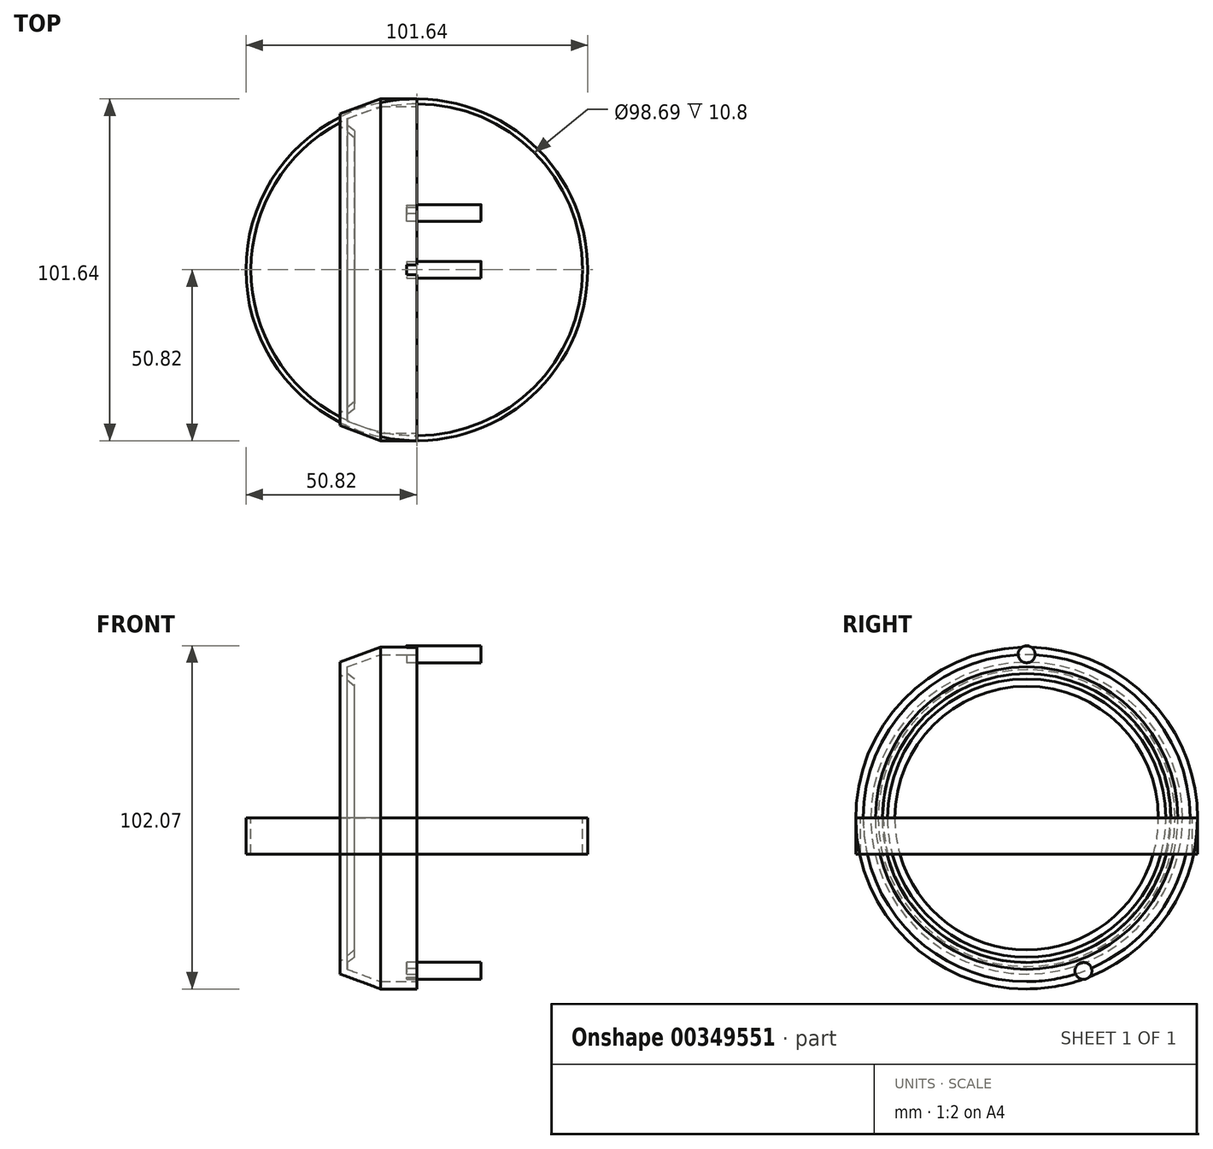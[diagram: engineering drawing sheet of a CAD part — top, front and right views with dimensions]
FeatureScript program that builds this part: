
annotation { "Feature Type Name" : "Feature", "Feature Type Description" : "" }
export const myFeature = defineFeature(function(context is Context, id is Id, definition is map)
    precondition{}
    {
        {
            var Q0;
            Q0=qCreatedBy(makeId("Top.planeOp"),FACE);
            var sketch = newSketch(context, id + "F0", { "sketchPlane" : qUnion([Q0])});
            skCircle(sketch, "E0", {"center": v(0, 0) * mm, "radius": 50.81 * mm});
            skCircle(sketch, "E1", {"center": v(0, 0) * mm, "radius": 49.34 * mm});
            skSolve(sketch);
        }
        {
            var Q0;
            Q0=makeQuery(id+"F0.imprint","IMPRINT",FACE,{"disambiguationData":[TD([[makeQuery(id+"F0.imprint","IMPRINT",EDGE,{"derivedFrom":sQuery(id+"F0.wireOp",EDGE,"E0")}),1.0]])]});
            extrude(context, id + "F1", {"entities" : qUnion([Q0]), "oppositeDirection" : true, "depth" : 10.8 * mm});
        }
        {
            var Q0;
            Q0=qCreatedBy(makeId("Front.planeOp"),FACE);
            var sketch = newSketch(context, id + "F2", { "sketchPlane" : qUnion([Q0])});
            skLineSegment(sketch, "E2", {"start": v(0, 50.81) * mm, "end": v(-10.8, 50.81) * mm});
            skLineSegment(sketch, "E3", {"start": v(-10.8, 48.62) * mm, "end": v(0, 48.62) * mm});
            skLineSegment(sketch, "E4", {"start": v(0, 48.62) * mm, "end": v(0, 50.81) * mm});
            skLineSegment(sketch, "E5", {"start": v(-10.8, 50.81) * mm, "end": v(-22.8, 46.36) * mm});
            skLineSegment(sketch, "E6", {"start": v(-10.8, 48.62) * mm, "end": v(-22.8, 44.16) * mm});
            skLineSegment(sketch, "E7", {"start": v(-22.8, 44.16) * mm, "end": v(-22.8, 46.36) * mm});
            skLineSegment(sketch, "E8", {"start": v(-22.8, 46.36) * mm, "end": v(-22.8, 42.68) * mm});
            skLineSegment(sketch, "E9", {"start": v(-22.8, 42.68) * mm, "end": v(-18.54, 39.19) * mm});
            skLineSegment(sketch, "E10", {"start": v(-18.54, 39.19) * mm, "end": v(-18.54, 41.39) * mm});
            skLineSegment(sketch, "E11", {"start": v(-20.6, 44.16) * mm, "end": v(-20.6, 47.18) * mm});
            skLineSegment(sketch, "E12", {"start": v(-20.6, 47.18) * mm, "end": v(-20.6, 44.16) * mm});
            skLineSegment(sketch, "E13", {"start": v(-20.6, 47.18) * mm, "end": v(-20.67, 40.93) * mm});
            skLineSegment(sketch, "E14", {"start": v(-18.54, 41.39) * mm, "end": v(-22.8, 44.52) * mm});
            skLineSegment(sketch, "E15", {"start": v(0, 0) * mm, "end": v(-21.95, 0) * mm});
            skSolve(sketch);
        }
        {
            var Q0;
            {var subQ1=sQuery(id+"F2.wireOp",EDGE,"E2");Q0=makeQuery(id+"F2.imprint","IMPRINT",FACE,{"disambiguationData":[TD([[makeQuery(id+"F2.imprint","IMPRINT",EDGE,{"derivedFrom":subQ1}),1.0]])]});}
            var Q1;
            {var subQ5=sQuery(id+"F2.wireOp",EDGE,"E8");var subQ7=sQuery(id+"F2.wireOp",EDGE,"E6");var subQ8=makeQuery(id+"F2.imprint","INTERSECT",VERTEX,{"derivedFrom":[subQ7,subQ5]});Q1=makeQuery(id+"F2.imprint","IMPRINT",FACE,{"disambiguationData":[TD([[makeQuery(id+"F2.imprint","IMPRINT",EDGE,{"disambiguationData":[TD([[subQ8,1.0]])],"derivedFrom":subQ7}),1.0]])]});}
            var Q2;
            {var subQ0=sQuery(id+"F2.wireOp",EDGE,"E10");Q2=makeQuery(id+"F2.imprint","IMPRINT",FACE,{"disambiguationData":[TD([[makeQuery(id+"F2.imprint","IMPRINT",EDGE,{"derivedFrom":subQ0}),1.0]])]});}
            var Q3;
            {var subQ0=sQuery(id+"F2.wireOp",EDGE,"E13");var subQ1=sQuery(id+"F2.wireOp",EDGE,"E6");var subQ2=makeQuery(id+"F2.imprint","INTERSECT",VERTEX,{"derivedFrom":[subQ1,subQ0]});Q3=makeQuery(id+"F2.imprint","IMPRINT",FACE,{"disambiguationData":[TD([[makeQuery(id+"F2.imprint","IMPRINT",EDGE,{"disambiguationData":[TD([[subQ2,-1.0]])],"derivedFrom":subQ1}),1.0]])]});}
            var Q4;
            {var subQ0=sQuery(id+"F2.wireOp",EDGE,"E13");var subQ3=sQuery(id+"F2.wireOp",EDGE,"E6");var subQ4=makeQuery(id+"F2.imprint","INTERSECT",VERTEX,{"derivedFrom":[subQ3,subQ0]});Q4=makeQuery(id+"F2.imprint","IMPRINT",FACE,{"disambiguationData":[TD([[makeQuery(id+"F2.imprint","IMPRINT",EDGE,{"disambiguationData":[TD([[subQ4,-1.0]])],"derivedFrom":subQ3}),-1.0]])]});}
            var Q5;
            {var subQ0=sQuery(id+"F2.wireOp",EDGE,"E8");var subQ1=sQuery(id+"F2.wireOp",EDGE,"E6");var subQ2=makeQuery(id+"F2.imprint","INTERSECT",VERTEX,{"derivedFrom":[subQ1,subQ0]});Q5=makeQuery(id+"F2.imprint","IMPRINT",FACE,{"disambiguationData":[TD([[makeQuery(id+"F2.imprint","IMPRINT",EDGE,{"disambiguationData":[TD([[subQ2,1.0]])],"derivedFrom":subQ1}),-1.0]])]});}
            var Q6;
            {var subQ0=sQuery(id+"F2.wireOp",EDGE,"E7");Q6=makeQuery(id+"F2.imprint","IMPRINT",FACE,{"disambiguationData":[TD([[makeQuery(id+"F2.imprint","IMPRINT",EDGE,{"derivedFrom":subQ0}),-1.0]])]});}
            var Q7;
            {var subQ0=sQuery(id+"F2.wireOp",EDGE,"E12");var subQ1=sQuery(id+"F2.wireOp",EDGE,"E6");var subQ2=makeQuery(id+"F2.imprint","INTERSECT",VERTEX,{"derivedFrom":[subQ1,subQ0]});Q7=makeQuery(id+"F2.imprint","IMPRINT",FACE,{"disambiguationData":[TD([[makeQuery(id+"F2.imprint","IMPRINT",EDGE,{"disambiguationData":[TD([[subQ2,-1.0]])],"derivedFrom":subQ1}),-1.0]])]});}
            var Q8;
            Q8=sQuery(id+"F2.wireOp",EDGE,"E15");
            revolve(context, id + "F3", {"entities" : qUnion([Q0, Q1, Q2, Q3, Q4, Q5, Q6, Q7]), "axis" : qUnion([Q8]), "revolveType" : RevolveType.FULL});
        }
        {
            var Q0;
            Q0=qCreatedBy(makeId("Right.planeOp"),FACE);
            var sketch = newSketch(context, id + "F4", { "sketchPlane" : qUnion([Q0])});
            skCircle(sketch, "E16", {"center": v(0, 48.72) * mm, "radius": 2.52 * mm});
            skSolve(sketch);
        }
        {
            var Q0;
            Q0=makeQuery(id+"F4.imprint","IMPRINT",FACE,{"disambiguationData":[TD([[makeQuery(id+"F4.imprint","IMPRINT",EDGE,{"derivedFrom":sQuery(id+"F4.wireOp",EDGE,"E16")}),1.0]])]});
            extrude(context, id + "F5", {"entities" : qUnion([Q0]), "operationType" : NewBodyOperationType.ADD, "depth" : 18.8 * mm});
        }
        {
            var Q0;
            Q0 = qSketchRegion(id + "F4", true);
            extrude(context, id + "F6", {"entities" : qUnion([Q0]), "operationType" : NewBodyOperationType.ADD, "oppositeDirection" : true, "depth" : 3.05 * mm});
        }
        {
            var Q0;
            Q0=qCreatedBy(makeId("Right.planeOp"),FACE);
            var sketch = newSketch(context, id + "F7", { "sketchPlane" : qUnion([Q0])});
            skCircle(sketch, "E17", {"center": v(16.89, -45.44) * mm, "radius": 2.52 * mm});
            skSolve(sketch);
        }
        {
            var Q0;
            Q0=makeQuery(id+"F7.imprint","IMPRINT",FACE,{"disambiguationData":[TD([[makeQuery(id+"F7.imprint","IMPRINT",EDGE,{"derivedFrom":sQuery(id+"F7.wireOp",EDGE,"E17")}),1.0]])]});
            extrude(context, id + "F8", {"entities" : qUnion([Q0]), "operationType" : NewBodyOperationType.ADD, "depth" : 19.1 * mm});
        }
        {
            var Q0;
            Q0 = qSketchRegion(id + "F7", true);
            extrude(context, id + "F9", {"entities" : qUnion([Q0]), "operationType" : NewBodyOperationType.ADD, "oppositeDirection" : true, "depth" : 3.05 * mm});
        }
        {
            var Q0;
            Q0 = qSketchRegion(id + "F4", true);
            extrude(context, id + "F10", {"entities" : qUnion([Q0]), "operationType" : NewBodyOperationType.ADD, "depth" : 19.1 * mm});
        }
    });
